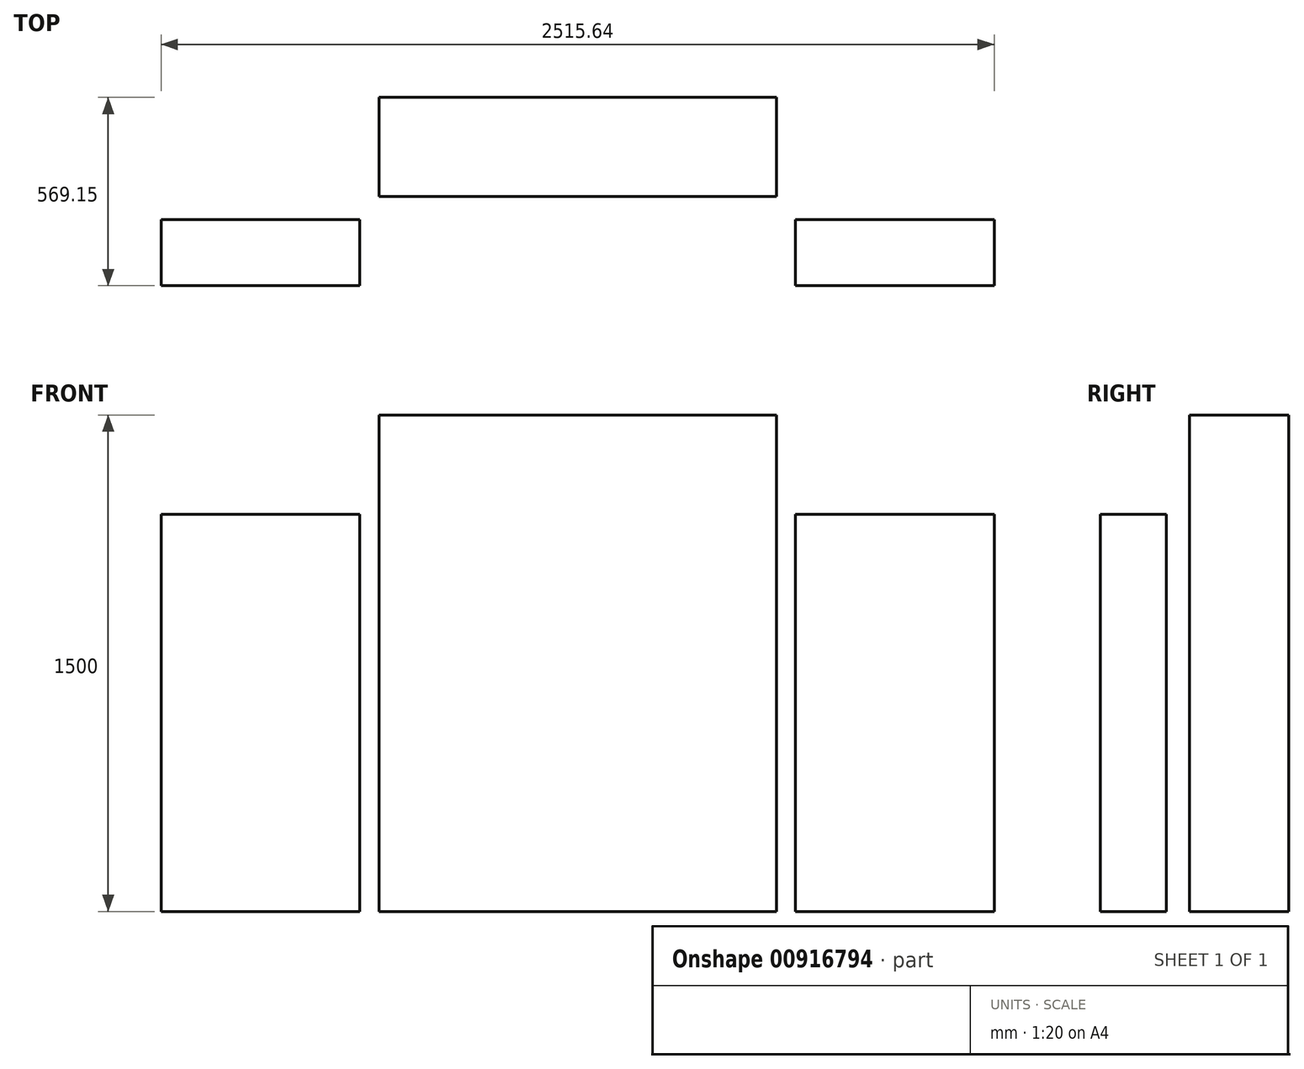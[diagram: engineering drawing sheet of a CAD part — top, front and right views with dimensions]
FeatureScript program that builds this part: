
annotation { "Feature Type Name" : "Feature", "Feature Type Description" : "" }
export const myFeature = defineFeature(function(context is Context, id is Id, definition is map)
    precondition{}
    {
        {
            var Q0;
            Q0=qCreatedBy(makeId("Top.planeOp"),FACE);
            var sketch = newSketch(context, id + "F0", { "sketchPlane" : qUnion([Q0])});
            skLineSegment(sketch, "E0.bottom", {"start": v(600, -150) * mm, "end": v(-600, -150) * mm});
            skLineSegment(sketch, "E0.top", {"start": v(600, 150) * mm, "end": v(-600, 150) * mm});
            skLineSegment(sketch, "E0.left", {"start": v(600, -150) * mm, "end": v(600, 150) * mm});
            skLineSegment(sketch, "E0.right", {"start": v(-600, -150) * mm, "end": v(-600, 150) * mm});
            skPoint(sketch, "E0.middle", {"position": v(0, 0) * mm});
            skLineSegment(sketch, "E1", {"start": v(0, 0) * mm, "end": v(0, -649.42) * mm, "construction": true});
            skLineSegment(sketch, "E2.bottom", {"start": v(-657.82, -219.15) * mm, "end": v(-1257.82, -219.15) * mm});
            skLineSegment(sketch, "E2.top", {"start": v(-657.82, -419.15) * mm, "end": v(-1257.82, -419.15) * mm});
            skLineSegment(sketch, "E2.left", {"start": v(-657.82, -219.15) * mm, "end": v(-657.82, -419.15) * mm});
            skLineSegment(sketch, "E2.right", {"start": v(-1257.82, -219.15) * mm, "end": v(-1257.82, -419.15) * mm});
            skLineSegment(sketch, "E3.MirrorCS", {"start": v(1257.82, -219.15) * mm, "end": v(1257.82, -419.15) * mm});
            skLineSegment(sketch, "E4.MirrorCS", {"start": v(657.82, -419.15) * mm, "end": v(1257.82, -419.15) * mm});
            skLineSegment(sketch, "E5.MirrorCS", {"start": v(657.82, -219.15) * mm, "end": v(1257.82, -219.15) * mm});
            skLineSegment(sketch, "E6.MirrorCS", {"start": v(657.82, -219.15) * mm, "end": v(657.82, -419.15) * mm});
            skSolve(sketch);
        }
        {
            var Q0;
            Q0=makeQuery(id+"F0.imprint","IMPRINT",FACE,{"disambiguationData":[TD([[makeQuery(id+"F0.imprint","IMPRINT",EDGE,{"derivedFrom":sQuery(id+"F0.wireOp",EDGE,"E0.bottom")}),-1.0]])]});
            extrude(context, id + "F1", {"entities" : qUnion([Q0]), "depth" : 1500 * mm, "offsetDistance" : 25 * mm});
        }
        {
            var Q0;
            Q0=qCreatedBy(makeId("Top.planeOp"),FACE);
            var sketch = newSketch(context, id + "F2", { "sketchPlane" : qUnion([Q0])});
            skLineSegment(sketch, "E7.0", {"start": v(-657.82, -219.15) * mm, "end": v(-1257.82, -219.15) * mm});
            skLineSegment(sketch, "E7.1", {"start": v(-1257.82, -219.15) * mm, "end": v(-1257.82, -419.15) * mm});
            skLineSegment(sketch, "E7.2", {"start": v(-657.82, -419.15) * mm, "end": v(-1257.82, -419.15) * mm});
            skLineSegment(sketch, "E7.3", {"start": v(-657.82, -219.15) * mm, "end": v(-657.82, -419.15) * mm});
            skLineSegment(sketch, "E7.4", {"start": v(657.82, -219.15) * mm, "end": v(1257.82, -219.15) * mm});
            skLineSegment(sketch, "E7.5", {"start": v(657.82, -419.15) * mm, "end": v(1257.82, -419.15) * mm});
            skLineSegment(sketch, "E7.6", {"start": v(657.82, -219.15) * mm, "end": v(657.82, -419.15) * mm});
            skLineSegment(sketch, "E8.0", {"start": v(1257.82, -219.15) * mm, "end": v(1257.82, -419.15) * mm});
            skSolve(sketch);
        }
        {
            var Q0;
            Q0 = qSketchRegion(id + "F2", true);
            extrude(context, id + "F3", {"entities" : qUnion([Q0]), "depth" : 1200 * mm, "offsetDistance" : 25 * mm});
        }
    });
